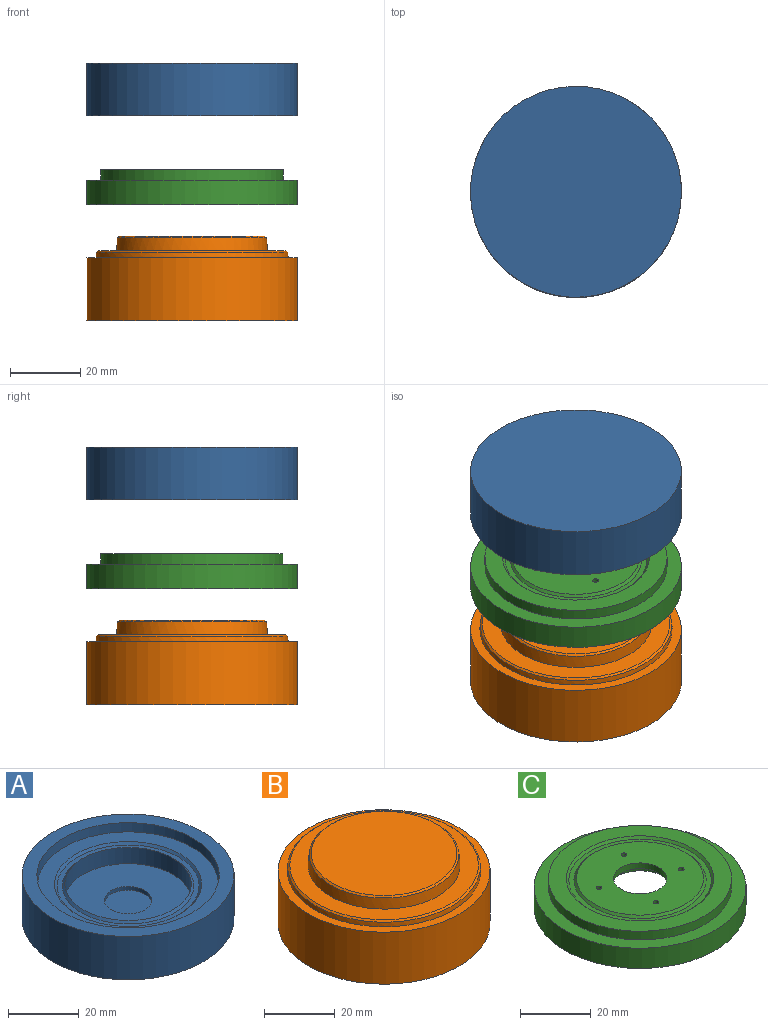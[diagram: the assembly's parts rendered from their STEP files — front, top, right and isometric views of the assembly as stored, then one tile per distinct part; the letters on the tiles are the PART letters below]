
ASSEMBLY  parts=3 mates=2
PART A: 12 faces, bbox 60x60x15 mm
  f0: cylinder r=30mm len=60mm, axis (0,0,-1), area 2827.4mm2, adj f1,f2
  f1: plane 60x60mm, normal (0,0,1), area 736.3mm2, adj f0,f3
  f2: plane 60x60mm, normal (0,0,-1), area 2827.4mm2, adj f0
  f3: cone r=25.8mm half-angle=5deg, axis (0,0,1), area 485.7mm2, adj f1,f4
  f4: plane 51.08x51.08mm, normal (0,0,1), area 689.7mm2, adj f3,f6
  f5: cone r=17.9mm half-angle=45deg, axis (0,0,-1), area 113.5mm2, adj f7,f11
  f6: cone r=20.8mm half-angle=45deg, axis (0,0,1), area 127.2mm2, adj f4,f7
  f7: plane 40.2x40.2mm, normal (0,0,1), area 182.4mm2, adj f5,f6
  f8: plane 13.4x13.4mm, normal (0,0,1), area 141mm2, adj f9
  f9: cylinder r=6.7mm len=13.4mm, axis (0,0,1), area 54.7mm2, adj f8,f10
  f10: plane 35.8x35.8mm, normal (0,0,1), area 865.6mm2, adj f9,f11
  f11: cylinder r=17.9mm len=35.8mm, axis (0,0,1), area 629.8mm2, adj f5,f10
PART B: 12 faces, bbox 60x60x24.1 mm
  f0: cylinder r=30mm len=60mm, axis (0,0,-1), area 3392.9mm2, adj f1,f2
  f1: plane 60x60mm, normal (0,0,1), area 477.5mm2, adj f0,f3
  f2: plane 60x60mm, normal (0,0,-1), area 2788.9mm2, adj f0,f11
  f3: cone r=27.35mm half-angle=5deg, axis (0,0,-1), area 258.5mm2, adj f1,f5
  f4: plane 53.35x53.35mm, normal (0,0,1), area 783.2mm2, adj f5,f6
  f5: cone r=26.68mm half-angle=47.5deg, axis (0,0,-1), area 124.8mm2, adj f3,f4
  f6: cone r=21.5mm half-angle=5deg, axis (0,0,-1), area 484.9mm2, adj f4,f8
  f7: plane 41.28x41.28mm, normal (0,0,1), area 1338.5mm2, adj f8
  f8: cone r=20.64mm half-angle=47.5deg, axis (0,0,-1), area 96.9mm2, adj f6,f7
  f9: cylinder r=3.25mm len=6.5mm, axis (0,0,-1), area 97mm2, adj f10,f11
  f10: plane 6.5x6.5mm, normal (0,0,-1), area 33.2mm2, adj f9
  f11: cone r=3.25mm half-angle=45deg, axis (0,0,-1), area 7.5mm2, adj f2,f9
PART C: 20 faces, bbox 60x60x10 mm
  f0: plane 36x36mm, normal (0,0,1), area 830.7mm2, adj f1,f13,f14,f15,f16,f17
  f1: cylinder r=7.55mm len=15.11mm, axis (0,0,1), area 94.9mm2, adj f0,f11
  f2: plane 60x60mm, normal (0,0,-1), area 477.5mm2, adj f3,f7
  f3: cylinder r=30mm len=60mm, axis (0,0,-1), area 1319.5mm2, adj f2,f4
  f4: plane 60x60mm, normal (0,0,1), area 716mm2, adj f3,f5
  f5: cylinder r=25.93mm len=51.85mm, axis (0,0,-1), area 488.7mm2, adj f4,f6
  f6: plane 51.85x51.85mm, normal (0,0,1), area 745.8mm2, adj f5,f18
  f7: cylinder r=27.35mm len=54.7mm, axis (0,0,-1), area 343.7mm2, adj f2,f8
  f8: plane 54.7x54.7mm, normal (0,0,-1), area 918mm2, adj f7,f10
  f9: plane 42.7x42.7mm, normal (0,0,-1), area 1149.5mm2, adj f10,f12,f13,f14,f15,f16
  f10: cylinder r=21.35mm len=42.7mm, axis (0,0,-1), area 536.6mm2, adj f8,f9
  f11: plane 18.7x18.7mm, normal (0,0,-1), area 95.3mm2, adj f1,f12
  f12: cylinder r=9.35mm len=18.7mm, axis (0,0,-1), area 117.5mm2, adj f9,f11
  f13: cylinder r=0.79mm len=4mm, axis (0,0,1), area 19.9mm2, adj f0,f9
  f14: cylinder r=0.79mm len=4mm, axis (0,0,1), area 19.9mm2, adj f0,f9
  f15: cylinder r=0.79mm len=4mm, axis (0,0,1), area 19.9mm2, adj f0,f9
  f16: cylinder r=0.79mm len=4mm, axis (0,0,1), area 19.9mm2, adj f0,f9
  f17: cone r=18mm half-angle=45deg, axis (0,0,-1), area 114.1mm2, adj f0,f19
  f18: cone r=20.85mm half-angle=45deg, axis (0,0,1), area 127.5mm2, adj f6,f19
  f19: plane 40.3x40.3mm, normal (0,0,1), area 177mm2, adj f17,f18
PLACE A rot(axis=(0.98,0.18,0),180deg) t=(0,0,49.18)mm
PLACE B t=(0,0,-24.1)mm fixed
PLACE C rot(axis=(0,0,1),5.2deg) t=(0,0,8.88)mm
MATE cylindrical A.f0 <-> C.f1  axis (0,0,-1) through (0,0,37.18)mm
MATE cylindrical B.f0 <-> C.f1  axis (0,0,1) through (0,0,0)mm
